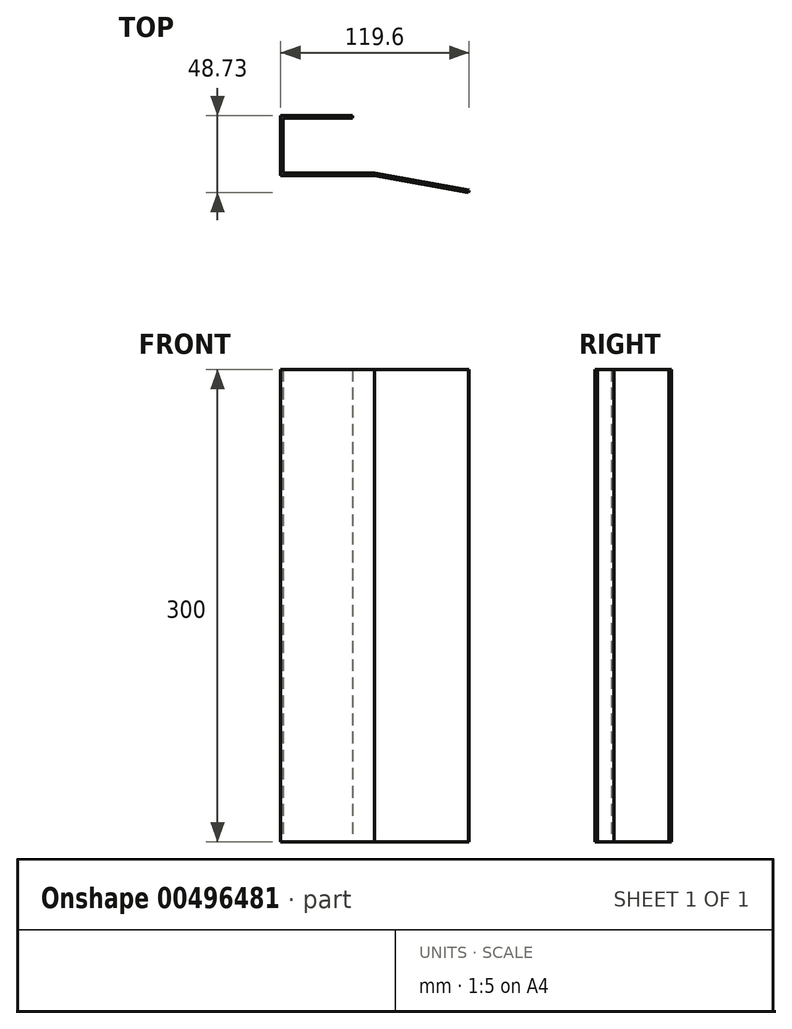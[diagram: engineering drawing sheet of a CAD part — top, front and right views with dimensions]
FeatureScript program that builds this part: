
annotation { "Feature Type Name" : "Feature", "Feature Type Description" : "" }
export const myFeature = defineFeature(function(context is Context, id is Id, definition is map)
    precondition{}
    {
        {
            var Q0;
            Q0=qCreatedBy(makeId("Top.planeOp"),FACE);
            var sketch = newSketch(context, id + "F0", { "sketchPlane" : qUnion([Q0])});
            skLineSegment(sketch, "E0", {"start": v(75.48, -3.93) * mm, "end": v(15.75, 6.6) * mm});
            skLineSegment(sketch, "E1", {"start": v(15.75, 6.6) * mm, "end": v(-43.85, 6.6) * mm});
            skLineSegment(sketch, "E2", {"start": v(-43.85, 6.6) * mm, "end": v(-43.85, 44.8) * mm});
            skLineSegment(sketch, "E3", {"start": v(-43.85, 44.8) * mm, "end": v(1.75, 44.8) * mm});
            skLineSegment(sketch, "E4", {"start": v(1.75, 44.8) * mm, "end": v(1.75, 43.2) * mm});
            skLineSegment(sketch, "E5", {"start": v(1.75, 43.2) * mm, "end": v(-42.25, 43.2) * mm});
            skLineSegment(sketch, "E6", {"start": v(-42.25, 43.2) * mm, "end": v(-42.25, 8.2) * mm});
            skLineSegment(sketch, "E7", {"start": v(-42.25, 8.2) * mm, "end": v(15.75, 8.2) * mm});
            skLineSegment(sketch, "E8", {"start": v(75.48, -3.93) * mm, "end": v(75.75, -2.35) * mm});
            skLineSegment(sketch, "E9", {"start": v(75.75, -2.35) * mm, "end": v(15.75, 8.2) * mm});
            skSolve(sketch);
        }
        {
            var Q0;
            Q0=makeQuery(id+"F0.imprint","IMPRINT",FACE,{"disambiguationData":[TD([[makeQuery(id+"F0.imprint","IMPRINT",EDGE,{"derivedFrom":sQuery(id+"F0.wireOp",EDGE,"E0")}),-1.0]])]});
            extrude(context, id + "F1", {"entities" : qUnion([Q0]), "depth" : 300 * mm});
        }
    });
